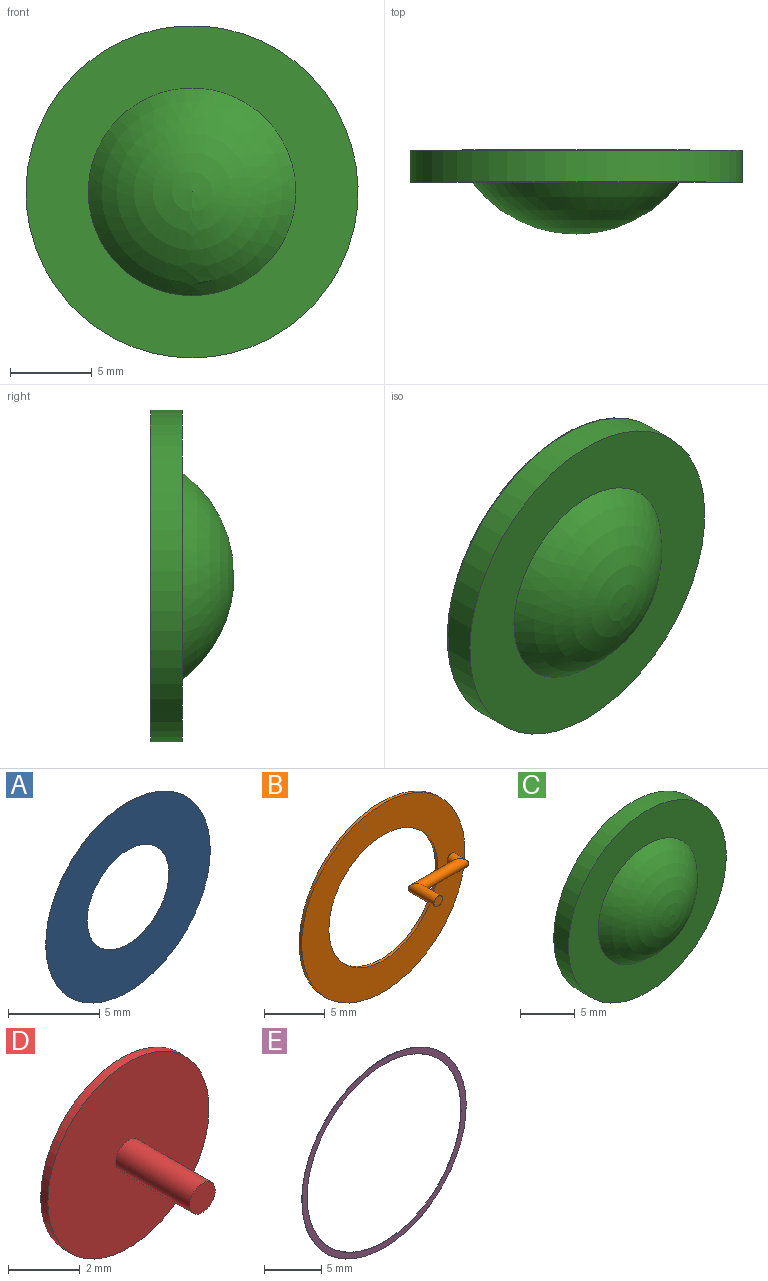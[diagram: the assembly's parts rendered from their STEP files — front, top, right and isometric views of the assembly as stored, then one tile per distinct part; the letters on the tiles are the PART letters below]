
ASSEMBLY  parts=5 mates=4
PART A: 4 faces, bbox 12.7x0x12.7 mm
  f0: cylinder r=3.17mm len=6.35mm, axis (0,-1,0), area 0.5mm2, adj f2,f3
  f1: cylinder r=6.35mm len=12.7mm, axis (0,-1,0), area 1mm2, adj f2,f3
  f2: plane 12.7x12.7mm, normal (0,1,0), area 95mm2, adj f0,f1
  f3: plane 12.7x12.7mm, normal (0,-1,0), area 95mm2, adj f0,f1
PART B: 8 faces, bbox 19.1x3.8x19.1 mm
  f0: cylinder r=0.5mm len=1.53mm, axis (0,-1,0), area 3.2mm2, adj f3,f6
  f1: plane 1x1mm, normal (0,-1,0), area 0.8mm2, adj f2
  f2: cylinder r=0.5mm len=3.03mm, axis (0,-1,0), area 7.9mm2, adj f1,f3
  f3: cylinder r=0.5mm len=6.08mm, axis (-1,0,0), area 16mm2, adj f0,f2
  f4: cylinder r=9.53mm len=19.05mm, axis (0,1,0), area 16.7mm2, adj f6,f7
  f5: cylinder r=6.35mm len=12.7mm, axis (0,1,0), area 11.1mm2, adj f6,f7
  f6: plane 19.05x19.05mm, normal (0,-1,0), area 157.6mm2, adj f0,f4,f5
  f7: plane 19.05x19.05mm, normal (0,1,0), area 158.3mm2, adj f4,f5
PART C: 16 faces, bbox 20.3x5.1x20.3 mm
  f0: sphere r=7.94mm, area 158.3mm2, adj f1
  f1: plane 20.32x20.32mm, normal (0,-1,0), area 197.6mm2, adj f0,f2
  f2: cylinder r=10.16mm len=20.32mm, axis (0,-1,0), area 121.6mm2, adj f1,f3
  f3: plane 20.32x20.32mm, normal (0,1,0), area 39.3mm2, adj f2,f4
  f4: cylinder r=9.53mm len=19.05mm, axis (0,1,0), area 15.2mm2, adj f3,f6
  f5: cylinder r=6.35mm len=12.7mm, axis (0,1,0), area 10.1mm2, adj f6,f7
  f6: plane 19.05x19.05mm, normal (0,1,0), area 157.6mm2, adj f4,f5,f13
  f7: plane 12.7x12.7mm, normal (0,1,0), area 95mm2, adj f5,f8
  f8: cylinder r=3.17mm len=6.35mm, axis (0,1,0), area 5.1mm2, adj f7,f9
  f9: plane 6.35x6.35mm, normal (0,1,0), area 30.9mm2, adj f8,f15
  f10: plane 1x1mm, normal (0,1,0), area 0.8mm2, adj f11
  f11: cylinder r=0.5mm len=3.03mm, axis (0,-1,0), area 7.9mm2, adj f10,f12
  f12: cylinder r=0.5mm len=6.08mm, axis (-1,0,0), area 16mm2, adj f11,f13
  f13: cylinder r=0.5mm len=1.53mm, axis (0,-1,0), area 3.2mm2, adj f6,f12
  f14: plane 1x1mm, normal (0,1,0), area 0.8mm2, adj f15
  f15: cylinder r=0.5mm len=2.92mm, axis (0,1,0), area 9.2mm2, adj f9,f14
PART D: 5 faces, bbox 6.4x3.2x6.4 mm
  f0: cylinder r=0.5mm len=2.92mm, axis (0,1,0), area 9.2mm2, adj f1,f3
  f1: plane 1x1mm, normal (0,-1,0), area 0.8mm2, adj f0
  f2: cylinder r=3.17mm len=6.35mm, axis (0,1,0), area 5.6mm2, adj f3,f4
  f3: plane 6.35x6.35mm, normal (0,-1,0), area 30.9mm2, adj f0,f2
  f4: plane 6.35x6.35mm, normal (0,1,0), area 31.7mm2, adj f2
PART E: 4 faces, bbox 20.3x0x20.3 mm
  f0: cylinder r=9.53mm len=19.05mm, axis (0,-1,0), area 1.5mm2, adj f2,f3
  f1: cylinder r=10.16mm len=20.32mm, axis (0,-1,0), area 1.6mm2, adj f2,f3
  f2: plane 20.32x20.32mm, normal (0,1,0), area 39.3mm2, adj f0,f1
  f3: plane 20.32x20.32mm, normal (0,-1,0), area 39.3mm2, adj f0,f1
PLACE A t=(0,88.92,0)mm
PLACE B t=(-0.04,88.92,0)mm
PLACE C t=(0,88.92,0)mm
PLACE D t=(0,88.92,0)mm
PLACE E t=(0,88.95,0)mm
MATE fastened B.f4 <-> C.f9  axis (0,-1,0) through (-0.04,-0.28,0)mm
MATE fastened D.f0 <-> C.f8  axis (0,-1,0) through (0,-0.28,0)mm
MATE fastened E.f0 <-> A.f1  axis (0,-1,0) through (0,0,0)mm
MATE fastened A.f1 <-> C.f4  axis (0,-1,0) through (0,-0.03,0)mm
